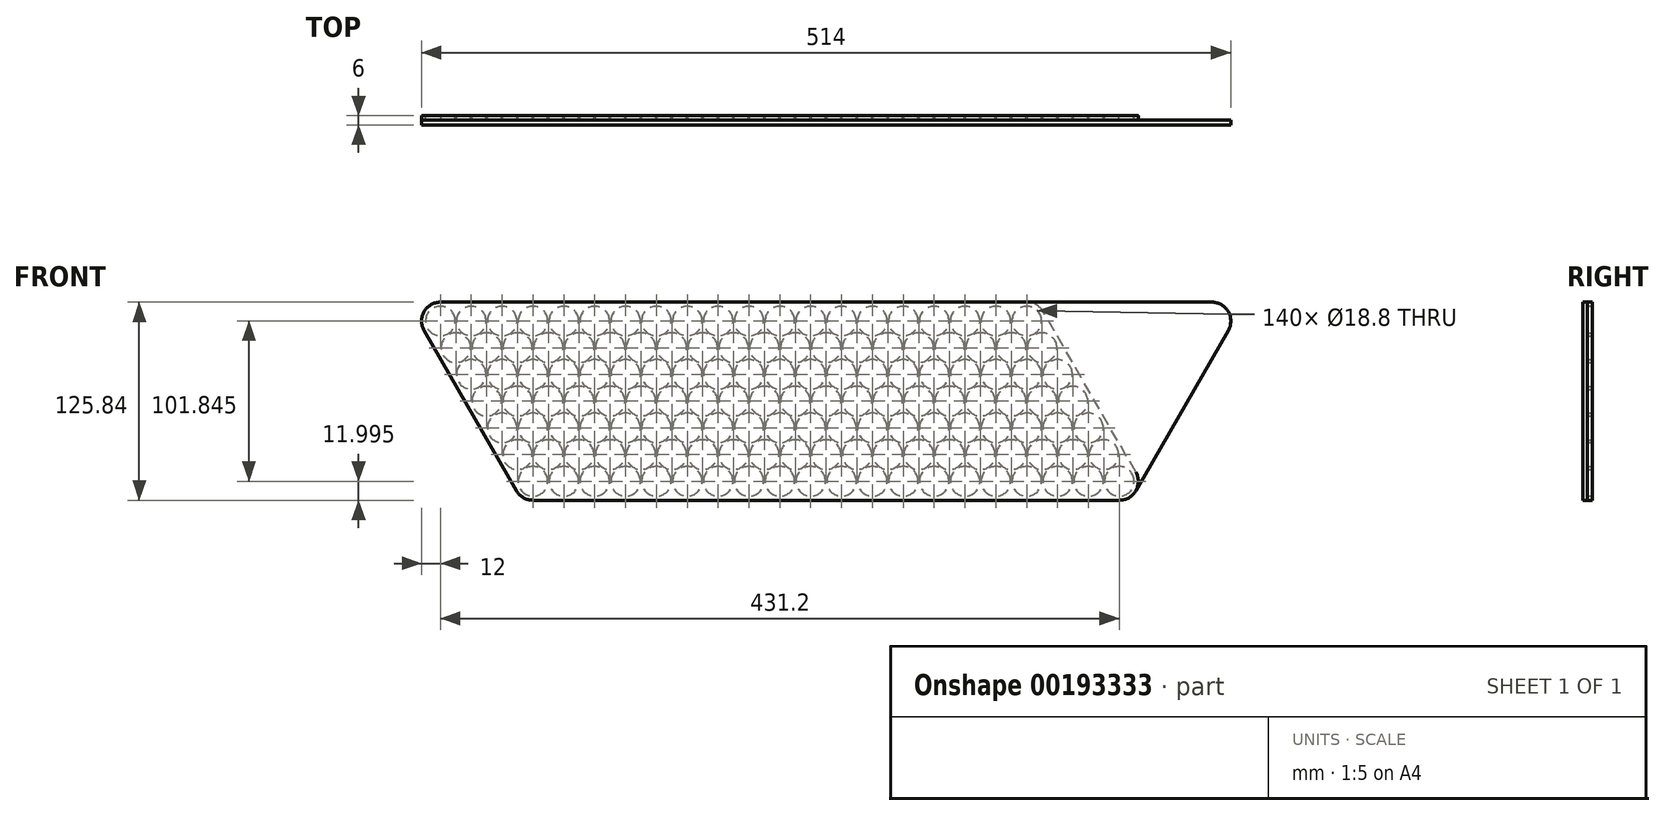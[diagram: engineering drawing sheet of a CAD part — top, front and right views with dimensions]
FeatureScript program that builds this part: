
annotation { "Feature Type Name" : "Feature", "Feature Type Description" : "" }
export const myFeature = defineFeature(function(context is Context, id is Id, definition is map)
    precondition{}
    {
        {
            var Q0;
            Q0=qCreatedBy(makeId("Front.planeOp"),FACE);
            var sketch = newSketch(context, id + "F0", { "sketchPlane" : qUnion([Q0])});
            skLineSegment(sketch, "E0", {"start": v(0, 0) * mm, "end": v(79.44, 0) * mm, "construction": true});
            skLineSegment(sketch, "E1", {"start": v(0, 0) * mm, "end": v(43.4, -75.16) * mm, "construction": true});
            skCircle(sketch, "E2", {"center": v(0, 0) * mm, "radius": 9.4 * mm});
            skCircle(sketch, "E3.1.0.0", {"center": v(19.6, 0) * mm, "radius": 9.4 * mm});
            skCircle(sketch, "E3.2.0.0", {"center": v(39.2, 0) * mm, "radius": 9.4 * mm});
            skCircle(sketch, "E3.3.0.0", {"center": v(58.8, 0) * mm, "radius": 9.4 * mm});
            skCircle(sketch, "E3.4.0.0", {"center": v(78.4, 0) * mm, "radius": 9.4 * mm});
            skCircle(sketch, "E3.5.0.0", {"center": v(98, 0) * mm, "radius": 9.4 * mm});
            skCircle(sketch, "E3.6.0.0", {"center": v(117.6, 0) * mm, "radius": 9.4 * mm});
            skCircle(sketch, "E3.7.0.0", {"center": v(137.2, 0) * mm, "radius": 9.4 * mm});
            skCircle(sketch, "E3.8.0.0", {"center": v(156.8, 0) * mm, "radius": 9.4 * mm});
            skCircle(sketch, "E3.9.0.0", {"center": v(176.4, 0) * mm, "radius": 9.4 * mm});
            skCircle(sketch, "E3.10.0.0", {"center": v(196, 0) * mm, "radius": 9.4 * mm});
            skCircle(sketch, "E3.11.0.0", {"center": v(215.6, 0) * mm, "radius": 9.4 * mm});
            skCircle(sketch, "E3.12.0.0", {"center": v(235.2, 0) * mm, "radius": 9.4 * mm});
            skCircle(sketch, "E3.13.0.0", {"center": v(254.8, 0) * mm, "radius": 9.4 * mm});
            skCircle(sketch, "E3.14.0.0", {"center": v(274.4, 0) * mm, "radius": 9.4 * mm});
            skCircle(sketch, "E3.15.0.0", {"center": v(294, 0) * mm, "radius": 9.4 * mm});
            skCircle(sketch, "E3.16.0.0", {"center": v(313.6, 0) * mm, "radius": 9.4 * mm});
            skCircle(sketch, "E3.17.0.0", {"center": v(333.2, 0) * mm, "radius": 9.4 * mm});
            skCircle(sketch, "E3.18.0.0", {"center": v(352.8, 0) * mm, "radius": 9.4 * mm});
            skCircle(sketch, "E3.19.0.0", {"center": v(372.4, 0) * mm, "radius": 9.4 * mm});
            skLineSegment(sketch, "E3.direction1", {"start": v(0, 0) * mm, "end": v(19.6, 0) * mm, "construction": true});
            skCircle(sketch, "E4.1.0.0", {"center": v(9.8, -16.97) * mm, "radius": 9.4 * mm});
            skCircle(sketch, "E4.2.0.0", {"center": v(19.6, -33.95) * mm, "radius": 9.4 * mm});
            skCircle(sketch, "E4.3.0.0", {"center": v(29.4, -50.92) * mm, "radius": 9.4 * mm});
            skCircle(sketch, "E4.4.0.0", {"center": v(39.2, -67.9) * mm, "radius": 9.4 * mm});
            skCircle(sketch, "E4.5.0.0", {"center": v(49, -84.87) * mm, "radius": 9.4 * mm});
            skCircle(sketch, "E4.6.0.0", {"center": v(58.8, -101.84) * mm, "radius": 9.4 * mm});
            skLineSegment(sketch, "E4.direction1", {"start": v(0, 0) * mm, "end": v(9.8, -16.97) * mm, "construction": true});
            skCircle(sketch, "E5.1.0.0", {"center": v(29.4, -16.97) * mm, "radius": 9.4 * mm});
            skCircle(sketch, "E5.1.0.1", {"center": v(39.2, -33.95) * mm, "radius": 9.4 * mm});
            skCircle(sketch, "E5.1.0.2", {"center": v(49, -50.92) * mm, "radius": 9.4 * mm});
            skCircle(sketch, "E5.1.0.3", {"center": v(58.8, -67.9) * mm, "radius": 9.4 * mm});
            skCircle(sketch, "E5.1.0.4", {"center": v(68.6, -84.87) * mm, "radius": 9.4 * mm});
            skCircle(sketch, "E5.1.0.5", {"center": v(78.4, -101.84) * mm, "radius": 9.4 * mm});
            skCircle(sketch, "E5.2.0.0", {"center": v(49, -16.97) * mm, "radius": 9.4 * mm});
            skCircle(sketch, "E5.2.0.1", {"center": v(58.8, -33.95) * mm, "radius": 9.4 * mm});
            skCircle(sketch, "E5.2.0.2", {"center": v(68.6, -50.92) * mm, "radius": 9.4 * mm});
            skCircle(sketch, "E5.2.0.3", {"center": v(78.4, -67.9) * mm, "radius": 9.4 * mm});
            skCircle(sketch, "E5.2.0.4", {"center": v(88.2, -84.87) * mm, "radius": 9.4 * mm});
            skCircle(sketch, "E5.2.0.5", {"center": v(98, -101.84) * mm, "radius": 9.4 * mm});
            skCircle(sketch, "E5.3.0.0", {"center": v(68.6, -16.97) * mm, "radius": 9.4 * mm});
            skCircle(sketch, "E5.3.0.1", {"center": v(78.4, -33.95) * mm, "radius": 9.4 * mm});
            skCircle(sketch, "E5.3.0.2", {"center": v(88.2, -50.92) * mm, "radius": 9.4 * mm});
            skCircle(sketch, "E5.3.0.3", {"center": v(98, -67.9) * mm, "radius": 9.4 * mm});
            skCircle(sketch, "E5.3.0.4", {"center": v(107.8, -84.87) * mm, "radius": 9.4 * mm});
            skCircle(sketch, "E5.3.0.5", {"center": v(117.6, -101.84) * mm, "radius": 9.4 * mm});
            skCircle(sketch, "E5.4.0.0", {"center": v(88.2, -16.97) * mm, "radius": 9.4 * mm});
            skCircle(sketch, "E5.4.0.1", {"center": v(98, -33.95) * mm, "radius": 9.4 * mm});
            skCircle(sketch, "E5.4.0.2", {"center": v(107.8, -50.92) * mm, "radius": 9.4 * mm});
            skCircle(sketch, "E5.4.0.3", {"center": v(117.6, -67.9) * mm, "radius": 9.4 * mm});
            skCircle(sketch, "E5.4.0.4", {"center": v(127.4, -84.87) * mm, "radius": 9.4 * mm});
            skCircle(sketch, "E5.4.0.5", {"center": v(137.2, -101.84) * mm, "radius": 9.4 * mm});
            skCircle(sketch, "E5.5.0.0", {"center": v(107.8, -16.97) * mm, "radius": 9.4 * mm});
            skCircle(sketch, "E5.5.0.1", {"center": v(117.6, -33.95) * mm, "radius": 9.4 * mm});
            skCircle(sketch, "E5.5.0.2", {"center": v(127.4, -50.92) * mm, "radius": 9.4 * mm});
            skCircle(sketch, "E5.5.0.3", {"center": v(137.2, -67.9) * mm, "radius": 9.4 * mm});
            skCircle(sketch, "E5.5.0.4", {"center": v(147, -84.87) * mm, "radius": 9.4 * mm});
            skCircle(sketch, "E5.5.0.5", {"center": v(156.8, -101.84) * mm, "radius": 9.4 * mm});
            skCircle(sketch, "E5.6.0.0", {"center": v(127.4, -16.97) * mm, "radius": 9.4 * mm});
            skCircle(sketch, "E5.6.0.1", {"center": v(137.2, -33.95) * mm, "radius": 9.4 * mm});
            skCircle(sketch, "E5.6.0.2", {"center": v(147, -50.92) * mm, "radius": 9.4 * mm});
            skCircle(sketch, "E5.6.0.3", {"center": v(156.8, -67.9) * mm, "radius": 9.4 * mm});
            skCircle(sketch, "E5.6.0.4", {"center": v(166.6, -84.87) * mm, "radius": 9.4 * mm});
            skCircle(sketch, "E5.6.0.5", {"center": v(176.4, -101.84) * mm, "radius": 9.4 * mm});
            skCircle(sketch, "E5.7.0.0", {"center": v(147, -16.97) * mm, "radius": 9.4 * mm});
            skCircle(sketch, "E5.7.0.1", {"center": v(156.8, -33.95) * mm, "radius": 9.4 * mm});
            skCircle(sketch, "E5.7.0.2", {"center": v(166.6, -50.92) * mm, "radius": 9.4 * mm});
            skCircle(sketch, "E5.7.0.3", {"center": v(176.4, -67.9) * mm, "radius": 9.4 * mm});
            skCircle(sketch, "E5.7.0.4", {"center": v(186.2, -84.87) * mm, "radius": 9.4 * mm});
            skCircle(sketch, "E5.7.0.5", {"center": v(196, -101.84) * mm, "radius": 9.4 * mm});
            skCircle(sketch, "E5.8.0.0", {"center": v(166.6, -16.97) * mm, "radius": 9.4 * mm});
            skCircle(sketch, "E5.8.0.1", {"center": v(176.4, -33.95) * mm, "radius": 9.4 * mm});
            skCircle(sketch, "E5.8.0.2", {"center": v(186.2, -50.92) * mm, "radius": 9.4 * mm});
            skCircle(sketch, "E5.8.0.3", {"center": v(196, -67.9) * mm, "radius": 9.4 * mm});
            skCircle(sketch, "E5.8.0.4", {"center": v(205.8, -84.87) * mm, "radius": 9.4 * mm});
            skCircle(sketch, "E5.8.0.5", {"center": v(215.6, -101.84) * mm, "radius": 9.4 * mm});
            skCircle(sketch, "E5.9.0.0", {"center": v(186.2, -16.97) * mm, "radius": 9.4 * mm});
            skCircle(sketch, "E5.9.0.1", {"center": v(196, -33.95) * mm, "radius": 9.4 * mm});
            skCircle(sketch, "E5.9.0.2", {"center": v(205.8, -50.92) * mm, "radius": 9.4 * mm});
            skCircle(sketch, "E5.9.0.3", {"center": v(215.6, -67.9) * mm, "radius": 9.4 * mm});
            skCircle(sketch, "E5.9.0.4", {"center": v(225.4, -84.87) * mm, "radius": 9.4 * mm});
            skCircle(sketch, "E5.9.0.5", {"center": v(235.2, -101.84) * mm, "radius": 9.4 * mm});
            skCircle(sketch, "E5.10.0.0", {"center": v(205.8, -16.97) * mm, "radius": 9.4 * mm});
            skCircle(sketch, "E5.10.0.1", {"center": v(215.6, -33.95) * mm, "radius": 9.4 * mm});
            skCircle(sketch, "E5.10.0.2", {"center": v(225.4, -50.92) * mm, "radius": 9.4 * mm});
            skCircle(sketch, "E5.10.0.3", {"center": v(235.2, -67.9) * mm, "radius": 9.4 * mm});
            skCircle(sketch, "E5.10.0.4", {"center": v(245, -84.87) * mm, "radius": 9.4 * mm});
            skCircle(sketch, "E5.10.0.5", {"center": v(254.8, -101.84) * mm, "radius": 9.4 * mm});
            skCircle(sketch, "E5.11.0.0", {"center": v(225.4, -16.97) * mm, "radius": 9.4 * mm});
            skCircle(sketch, "E5.11.0.1", {"center": v(235.2, -33.95) * mm, "radius": 9.4 * mm});
            skCircle(sketch, "E5.11.0.2", {"center": v(245, -50.92) * mm, "radius": 9.4 * mm});
            skCircle(sketch, "E5.11.0.3", {"center": v(254.8, -67.9) * mm, "radius": 9.4 * mm});
            skCircle(sketch, "E5.11.0.4", {"center": v(264.6, -84.87) * mm, "radius": 9.4 * mm});
            skCircle(sketch, "E5.11.0.5", {"center": v(274.4, -101.84) * mm, "radius": 9.4 * mm});
            skCircle(sketch, "E5.12.0.0", {"center": v(245, -16.97) * mm, "radius": 9.4 * mm});
            skCircle(sketch, "E5.12.0.1", {"center": v(254.8, -33.95) * mm, "radius": 9.4 * mm});
            skCircle(sketch, "E5.12.0.2", {"center": v(264.6, -50.92) * mm, "radius": 9.4 * mm});
            skCircle(sketch, "E5.12.0.3", {"center": v(274.4, -67.9) * mm, "radius": 9.4 * mm});
            skCircle(sketch, "E5.12.0.4", {"center": v(284.2, -84.87) * mm, "radius": 9.4 * mm});
            skCircle(sketch, "E5.12.0.5", {"center": v(294, -101.84) * mm, "radius": 9.4 * mm});
            skCircle(sketch, "E5.13.0.0", {"center": v(264.6, -16.97) * mm, "radius": 9.4 * mm});
            skCircle(sketch, "E5.13.0.1", {"center": v(274.4, -33.95) * mm, "radius": 9.4 * mm});
            skCircle(sketch, "E5.13.0.2", {"center": v(284.2, -50.92) * mm, "radius": 9.4 * mm});
            skCircle(sketch, "E5.13.0.3", {"center": v(294, -67.9) * mm, "radius": 9.4 * mm});
            skCircle(sketch, "E5.13.0.4", {"center": v(303.8, -84.87) * mm, "radius": 9.4 * mm});
            skCircle(sketch, "E5.13.0.5", {"center": v(313.6, -101.84) * mm, "radius": 9.4 * mm});
            skCircle(sketch, "E5.14.0.0", {"center": v(284.2, -16.97) * mm, "radius": 9.4 * mm});
            skCircle(sketch, "E5.14.0.1", {"center": v(294, -33.95) * mm, "radius": 9.4 * mm});
            skCircle(sketch, "E5.14.0.2", {"center": v(303.8, -50.92) * mm, "radius": 9.4 * mm});
            skCircle(sketch, "E5.14.0.3", {"center": v(313.6, -67.9) * mm, "radius": 9.4 * mm});
            skCircle(sketch, "E5.14.0.4", {"center": v(323.4, -84.87) * mm, "radius": 9.4 * mm});
            skCircle(sketch, "E5.14.0.5", {"center": v(333.2, -101.84) * mm, "radius": 9.4 * mm});
            skCircle(sketch, "E5.15.0.0", {"center": v(303.8, -16.97) * mm, "radius": 9.4 * mm});
            skCircle(sketch, "E5.15.0.1", {"center": v(313.6, -33.95) * mm, "radius": 9.4 * mm});
            skCircle(sketch, "E5.15.0.2", {"center": v(323.4, -50.92) * mm, "radius": 9.4 * mm});
            skCircle(sketch, "E5.15.0.3", {"center": v(333.2, -67.9) * mm, "radius": 9.4 * mm});
            skCircle(sketch, "E5.15.0.4", {"center": v(343, -84.87) * mm, "radius": 9.4 * mm});
            skCircle(sketch, "E5.15.0.5", {"center": v(352.8, -101.84) * mm, "radius": 9.4 * mm});
            skCircle(sketch, "E5.16.0.0", {"center": v(323.4, -16.97) * mm, "radius": 9.4 * mm});
            skCircle(sketch, "E5.16.0.1", {"center": v(333.2, -33.95) * mm, "radius": 9.4 * mm});
            skCircle(sketch, "E5.16.0.2", {"center": v(343, -50.92) * mm, "radius": 9.4 * mm});
            skCircle(sketch, "E5.16.0.3", {"center": v(352.8, -67.9) * mm, "radius": 9.4 * mm});
            skCircle(sketch, "E5.16.0.4", {"center": v(362.6, -84.87) * mm, "radius": 9.4 * mm});
            skCircle(sketch, "E5.16.0.5", {"center": v(372.4, -101.84) * mm, "radius": 9.4 * mm});
            skCircle(sketch, "E5.17.0.0", {"center": v(343, -16.97) * mm, "radius": 9.4 * mm});
            skCircle(sketch, "E5.17.0.1", {"center": v(352.8, -33.95) * mm, "radius": 9.4 * mm});
            skCircle(sketch, "E5.17.0.2", {"center": v(362.6, -50.92) * mm, "radius": 9.4 * mm});
            skCircle(sketch, "E5.17.0.3", {"center": v(372.4, -67.9) * mm, "radius": 9.4 * mm});
            skCircle(sketch, "E5.17.0.4", {"center": v(382.2, -84.87) * mm, "radius": 9.4 * mm});
            skCircle(sketch, "E5.17.0.5", {"center": v(392, -101.84) * mm, "radius": 9.4 * mm});
            skCircle(sketch, "E5.18.0.0", {"center": v(362.6, -16.97) * mm, "radius": 9.4 * mm});
            skCircle(sketch, "E5.18.0.1", {"center": v(372.4, -33.95) * mm, "radius": 9.4 * mm});
            skCircle(sketch, "E5.18.0.2", {"center": v(382.2, -50.92) * mm, "radius": 9.4 * mm});
            skCircle(sketch, "E5.18.0.3", {"center": v(392, -67.9) * mm, "radius": 9.4 * mm});
            skCircle(sketch, "E5.18.0.4", {"center": v(401.8, -84.87) * mm, "radius": 9.4 * mm});
            skCircle(sketch, "E5.18.0.5", {"center": v(411.6, -101.84) * mm, "radius": 9.4 * mm});
            skCircle(sketch, "E5.19.0.0", {"center": v(382.2, -16.97) * mm, "radius": 9.4 * mm});
            skCircle(sketch, "E5.19.0.1", {"center": v(392, -33.95) * mm, "radius": 9.4 * mm});
            skCircle(sketch, "E5.19.0.2", {"center": v(401.8, -50.92) * mm, "radius": 9.4 * mm});
            skCircle(sketch, "E5.19.0.3", {"center": v(411.6, -67.9) * mm, "radius": 9.4 * mm});
            skCircle(sketch, "E5.19.0.4", {"center": v(421.4, -84.87) * mm, "radius": 9.4 * mm});
            skCircle(sketch, "E5.19.0.5", {"center": v(431.2, -101.84) * mm, "radius": 9.4 * mm});
            skLineSegment(sketch, "E5.direction1", {"start": v(9.8, -16.97) * mm, "end": v(29.4, -16.97) * mm, "construction": true});
            skLineSegment(sketch, "E6", {"start": v(0, 0) * mm, "end": v(372.4, 0) * mm, "construction": true});
            skLineSegment(sketch, "E7", {"start": v(372.4, 0) * mm, "end": v(441, -118.82) * mm, "construction": true});
            skLineSegment(sketch, "E8", {"start": v(441, -118.82) * mm, "end": v(68.6, -118.82) * mm, "construction": true});
            skLineSegment(sketch, "E9", {"start": v(68.6, -118.82) * mm, "end": v(0, 0) * mm, "construction": true});
            skArc(sketch, "E10", {"start": v(48.4, -107.84) * mm, "mid": v(52.8, -112.24) * mm, "end": v(58.8, -113.84) * mm});
            skArc(sketch, "E11", {"start": v(431.2, -113.84) * mm, "mid": v(441.6, -107.84) * mm, "end": v(441.6, -95.84) * mm});
            skArc(sketch, "E12", {"start": v(382.8, 6) * mm, "mid": v(378.4, 10.4) * mm, "end": v(372.4, 12) * mm});
            skArc(sketch, "E13", {"start": v(0, 12) * mm, "mid": v(-10.4, 6) * mm, "end": v(-10.4, -6) * mm});
            skLineSegment(sketch, "E14", {"start": v(0, 12) * mm, "end": v(372.4, 12) * mm});
            skLineSegment(sketch, "E15", {"start": v(-10.4, -6) * mm, "end": v(48.4, -107.84) * mm});
            skLineSegment(sketch, "E16", {"start": v(58.8, -113.84) * mm, "end": v(431.2, -113.84) * mm});
            skLineSegment(sketch, "E17", {"start": v(441.6, -95.84) * mm, "end": v(382.8, 6) * mm});
            skLineSegment(sketch, "E18", {"start": v(441.6, -107.84) * mm, "end": v(500.4, -6) * mm, "construction": true});
            skLineSegment(sketch, "E19", {"start": v(372.4, 12) * mm, "end": v(490, 12) * mm, "construction": true});
            skPoint(sketch, "E20.visualSharp", {"position": v(510.78, 12) * mm});
            skArc(sketch, "E20.filletArc", {"start": v(500.4, -6) * mm, "mid": v(500.4, 6) * mm, "end": v(490, 12) * mm, "construction": true});
            skSolve(sketch);
        }
        {
            var Q0;
            Q0=makeQuery(id+"F0.imprint","IMPRINT",FACE,{"disambiguationData":[TD([[makeQuery(id+"F0.imprint","IMPRINT",EDGE,{"derivedFrom":sQuery(id+"F0.wireOp",EDGE,"E2")}),-1.0]])]});
            extrude(context, id + "F1", {"entities" : qUnion([Q0]), "depth" : 3 * mm});
        }
        {
            var Q0;
            Q0=makeQuery(id+"F1.opExtrude","CAP_FACE",FACE,{"disambiguationData":[OSD([sQuery(id+"F0.wireOp",EDGE,"E2"),sQuery(id+"F0.wireOp",EDGE,"E3.1.0.0"),sQuery(id+"F0.wireOp",EDGE,"E3.2.0.0"),sQuery(id+"F0.wireOp",EDGE,"E3.3.0.0"),sQuery(id+"F0.wireOp",EDGE,"E3.4.0.0"),sQuery(id+"F0.wireOp",EDGE,"E3.5.0.0"),sQuery(id+"F0.wireOp",EDGE,"E3.6.0.0"),sQuery(id+"F0.wireOp",EDGE,"E3.7.0.0"),sQuery(id+"F0.wireOp",EDGE,"E3.8.0.0"),sQuery(id+"F0.wireOp",EDGE,"E3.9.0.0"),sQuery(id+"F0.wireOp",EDGE,"E3.10.0.0"),sQuery(id+"F0.wireOp",EDGE,"E3.11.0.0"),sQuery(id+"F0.wireOp",EDGE,"E3.12.0.0"),sQuery(id+"F0.wireOp",EDGE,"E3.13.0.0"),sQuery(id+"F0.wireOp",EDGE,"E3.14.0.0"),sQuery(id+"F0.wireOp",EDGE,"E3.15.0.0"),sQuery(id+"F0.wireOp",EDGE,"E3.16.0.0"),sQuery(id+"F0.wireOp",EDGE,"E3.17.0.0"),sQuery(id+"F0.wireOp",EDGE,"E3.18.0.0"),sQuery(id+"F0.wireOp",EDGE,"E3.19.0.0"),sQuery(id+"F0.wireOp",EDGE,"E4.1.0.0"),sQuery(id+"F0.wireOp",EDGE,"E4.2.0.0"),sQuery(id+"F0.wireOp",EDGE,"E4.3.0.0"),sQuery(id+"F0.wireOp",EDGE,"E4.4.0.0"),sQuery(id+"F0.wireOp",EDGE,"E4.5.0.0"),sQuery(id+"F0.wireOp",EDGE,"E4.6.0.0"),sQuery(id+"F0.wireOp",EDGE,"E5.1.0.0"),sQuery(id+"F0.wireOp",EDGE,"E5.1.0.1"),sQuery(id+"F0.wireOp",EDGE,"E5.1.0.2"),sQuery(id+"F0.wireOp",EDGE,"E5.1.0.3"),sQuery(id+"F0.wireOp",EDGE,"E5.1.0.4"),sQuery(id+"F0.wireOp",EDGE,"E5.1.0.5"),sQuery(id+"F0.wireOp",EDGE,"E5.2.0.0"),sQuery(id+"F0.wireOp",EDGE,"E5.2.0.1"),sQuery(id+"F0.wireOp",EDGE,"E5.2.0.2"),sQuery(id+"F0.wireOp",EDGE,"E5.2.0.3"),sQuery(id+"F0.wireOp",EDGE,"E5.2.0.4"),sQuery(id+"F0.wireOp",EDGE,"E5.2.0.5"),sQuery(id+"F0.wireOp",EDGE,"E5.3.0.0"),sQuery(id+"F0.wireOp",EDGE,"E5.3.0.1"),sQuery(id+"F0.wireOp",EDGE,"E5.3.0.2"),sQuery(id+"F0.wireOp",EDGE,"E5.3.0.3"),sQuery(id+"F0.wireOp",EDGE,"E5.3.0.4"),sQuery(id+"F0.wireOp",EDGE,"E5.3.0.5"),sQuery(id+"F0.wireOp",EDGE,"E5.4.0.0"),sQuery(id+"F0.wireOp",EDGE,"E5.4.0.1"),sQuery(id+"F0.wireOp",EDGE,"E5.4.0.2"),sQuery(id+"F0.wireOp",EDGE,"E5.4.0.3"),sQuery(id+"F0.wireOp",EDGE,"E5.4.0.4"),sQuery(id+"F0.wireOp",EDGE,"E5.4.0.5"),sQuery(id+"F0.wireOp",EDGE,"E5.5.0.0"),sQuery(id+"F0.wireOp",EDGE,"E5.5.0.1"),sQuery(id+"F0.wireOp",EDGE,"E5.5.0.2"),sQuery(id+"F0.wireOp",EDGE,"E5.5.0.3"),sQuery(id+"F0.wireOp",EDGE,"E5.5.0.4"),sQuery(id+"F0.wireOp",EDGE,"E5.5.0.5"),sQuery(id+"F0.wireOp",EDGE,"E5.6.0.0"),sQuery(id+"F0.wireOp",EDGE,"E5.6.0.1"),sQuery(id+"F0.wireOp",EDGE,"E5.6.0.2"),sQuery(id+"F0.wireOp",EDGE,"E5.6.0.3"),sQuery(id+"F0.wireOp",EDGE,"E5.6.0.4"),sQuery(id+"F0.wireOp",EDGE,"E5.6.0.5"),sQuery(id+"F0.wireOp",EDGE,"E5.7.0.0"),sQuery(id+"F0.wireOp",EDGE,"E5.7.0.1"),sQuery(id+"F0.wireOp",EDGE,"E5.7.0.2"),sQuery(id+"F0.wireOp",EDGE,"E5.7.0.3"),sQuery(id+"F0.wireOp",EDGE,"E5.7.0.4"),sQuery(id+"F0.wireOp",EDGE,"E5.7.0.5"),sQuery(id+"F0.wireOp",EDGE,"E5.8.0.0"),sQuery(id+"F0.wireOp",EDGE,"E5.8.0.1"),sQuery(id+"F0.wireOp",EDGE,"E5.8.0.2"),sQuery(id+"F0.wireOp",EDGE,"E5.8.0.3"),sQuery(id+"F0.wireOp",EDGE,"E5.8.0.4"),sQuery(id+"F0.wireOp",EDGE,"E5.8.0.5"),sQuery(id+"F0.wireOp",EDGE,"E5.9.0.0"),sQuery(id+"F0.wireOp",EDGE,"E5.9.0.1"),sQuery(id+"F0.wireOp",EDGE,"E5.9.0.2"),sQuery(id+"F0.wireOp",EDGE,"E5.9.0.3"),sQuery(id+"F0.wireOp",EDGE,"E5.9.0.4"),sQuery(id+"F0.wireOp",EDGE,"E5.9.0.5"),sQuery(id+"F0.wireOp",EDGE,"E5.10.0.0"),sQuery(id+"F0.wireOp",EDGE,"E5.10.0.1"),sQuery(id+"F0.wireOp",EDGE,"E5.10.0.2"),sQuery(id+"F0.wireOp",EDGE,"E5.10.0.3"),sQuery(id+"F0.wireOp",EDGE,"E5.10.0.4"),sQuery(id+"F0.wireOp",EDGE,"E5.10.0.5"),sQuery(id+"F0.wireOp",EDGE,"E5.11.0.0"),sQuery(id+"F0.wireOp",EDGE,"E5.11.0.1"),sQuery(id+"F0.wireOp",EDGE,"E5.11.0.2"),sQuery(id+"F0.wireOp",EDGE,"E5.11.0.3"),sQuery(id+"F0.wireOp",EDGE,"E5.11.0.4"),sQuery(id+"F0.wireOp",EDGE,"E5.11.0.5"),sQuery(id+"F0.wireOp",EDGE,"E5.12.0.0"),sQuery(id+"F0.wireOp",EDGE,"E5.12.0.1"),sQuery(id+"F0.wireOp",EDGE,"E5.12.0.2"),sQuery(id+"F0.wireOp",EDGE,"E5.12.0.3"),sQuery(id+"F0.wireOp",EDGE,"E5.12.0.4"),sQuery(id+"F0.wireOp",EDGE,"E5.12.0.5"),sQuery(id+"F0.wireOp",EDGE,"E5.13.0.0"),sQuery(id+"F0.wireOp",EDGE,"E5.13.0.1"),sQuery(id+"F0.wireOp",EDGE,"E5.13.0.2"),sQuery(id+"F0.wireOp",EDGE,"E5.13.0.3"),sQuery(id+"F0.wireOp",EDGE,"E5.13.0.4"),sQuery(id+"F0.wireOp",EDGE,"E5.13.0.5"),sQuery(id+"F0.wireOp",EDGE,"E5.14.0.0"),sQuery(id+"F0.wireOp",EDGE,"E5.14.0.1"),sQuery(id+"F0.wireOp",EDGE,"E5.14.0.2"),sQuery(id+"F0.wireOp",EDGE,"E5.14.0.3"),sQuery(id+"F0.wireOp",EDGE,"E5.14.0.4"),sQuery(id+"F0.wireOp",EDGE,"E5.14.0.5"),sQuery(id+"F0.wireOp",EDGE,"E5.15.0.0"),sQuery(id+"F0.wireOp",EDGE,"E5.15.0.1"),sQuery(id+"F0.wireOp",EDGE,"E5.15.0.2"),sQuery(id+"F0.wireOp",EDGE,"E5.15.0.3"),sQuery(id+"F0.wireOp",EDGE,"E5.15.0.4"),sQuery(id+"F0.wireOp",EDGE,"E5.15.0.5"),sQuery(id+"F0.wireOp",EDGE,"E5.16.0.0"),sQuery(id+"F0.wireOp",EDGE,"E5.16.0.1"),sQuery(id+"F0.wireOp",EDGE,"E5.16.0.2"),sQuery(id+"F0.wireOp",EDGE,"E5.16.0.3"),sQuery(id+"F0.wireOp",EDGE,"E5.16.0.4"),sQuery(id+"F0.wireOp",EDGE,"E5.16.0.5"),sQuery(id+"F0.wireOp",EDGE,"E5.17.0.0"),sQuery(id+"F0.wireOp",EDGE,"E5.17.0.1"),sQuery(id+"F0.wireOp",EDGE,"E5.17.0.2"),sQuery(id+"F0.wireOp",EDGE,"E5.17.0.3"),sQuery(id+"F0.wireOp",EDGE,"E5.17.0.4"),sQuery(id+"F0.wireOp",EDGE,"E5.17.0.5"),sQuery(id+"F0.wireOp",EDGE,"E5.18.0.0"),sQuery(id+"F0.wireOp",EDGE,"E5.18.0.1"),sQuery(id+"F0.wireOp",EDGE,"E5.18.0.2"),sQuery(id+"F0.wireOp",EDGE,"E5.18.0.3"),sQuery(id+"F0.wireOp",EDGE,"E5.18.0.4"),sQuery(id+"F0.wireOp",EDGE,"E5.18.0.5"),sQuery(id+"F0.wireOp",EDGE,"E5.19.0.0"),sQuery(id+"F0.wireOp",EDGE,"E5.19.0.1"),sQuery(id+"F0.wireOp",EDGE,"E5.19.0.2"),sQuery(id+"F0.wireOp",EDGE,"E5.19.0.3"),sQuery(id+"F0.wireOp",EDGE,"E5.19.0.4"),sQuery(id+"F0.wireOp",EDGE,"E5.19.0.5"),sQuery(id+"F0.wireOp",EDGE,"E10"),sQuery(id+"F0.wireOp",EDGE,"E11"),sQuery(id+"F0.wireOp",EDGE,"E13"),sQuery(id+"F0.wireOp",EDGE,"E14"),sQuery(id+"F0.wireOp",EDGE,"E15"),sQuery(id+"F0.wireOp",EDGE,"E16"),sQuery(id+"F0.wireOp",EDGE,"E18"),sQuery(id+"F0.wireOp",EDGE,"E19"),sQuery(id+"F0.wireOp",EDGE,"E20.filletArc")])],"isStart":false});
            var sketch = newSketch(context, id + "F2", { "sketchPlane" : qUnion([Q0])});
            skLineSegment(sketch, "E21.0", {"start": v(0, 12) * mm, "end": v(490, 12) * mm});
            skArc(sketch, "E21.1", {"start": v(0, 12) * mm, "mid": v(-10.4, 6) * mm, "end": v(-10.4, -6) * mm});
            skLineSegment(sketch, "E21.2", {"start": v(-10.4, -6) * mm, "end": v(48.4, -107.84) * mm});
            skArc(sketch, "E21.3", {"start": v(48.4, -107.84) * mm, "mid": v(52.8, -112.24) * mm, "end": v(58.8, -113.84) * mm});
            skLineSegment(sketch, "E21.4", {"start": v(58.8, -113.84) * mm, "end": v(431.2, -113.84) * mm});
            skLineSegment(sketch, "E21.5", {"start": v(431.2, -113.84) * mm, "end": v(431.2, -113.84) * mm});
            skLineSegment(sketch, "E22", {"start": v(441.6, -107.84) * mm, "end": v(500.4, -6) * mm});
            skArc(sketch, "E23", {"start": v(431.2, -113.84) * mm, "mid": v(437.2, -112.24) * mm, "end": v(441.6, -107.84) * mm});
            skPoint(sketch, "E24.orphan", {"position": v(562.43, 12) * mm});
            skPoint(sketch, "E25.visualSharp", {"position": v(510.78, 12) * mm});
            skArc(sketch, "E25.filletArc", {"start": v(500.4, -6) * mm, "mid": v(500.4, 6) * mm, "end": v(490, 12) * mm});
            skSolve(sketch);
        }
        {
            var Q0;
            Q0=qSketchRegion(id+"F2",true);
            extrude(context, id + "F3", {"entities" : qUnion([Q0]), "depth" : 3 * mm});
        }
    });
